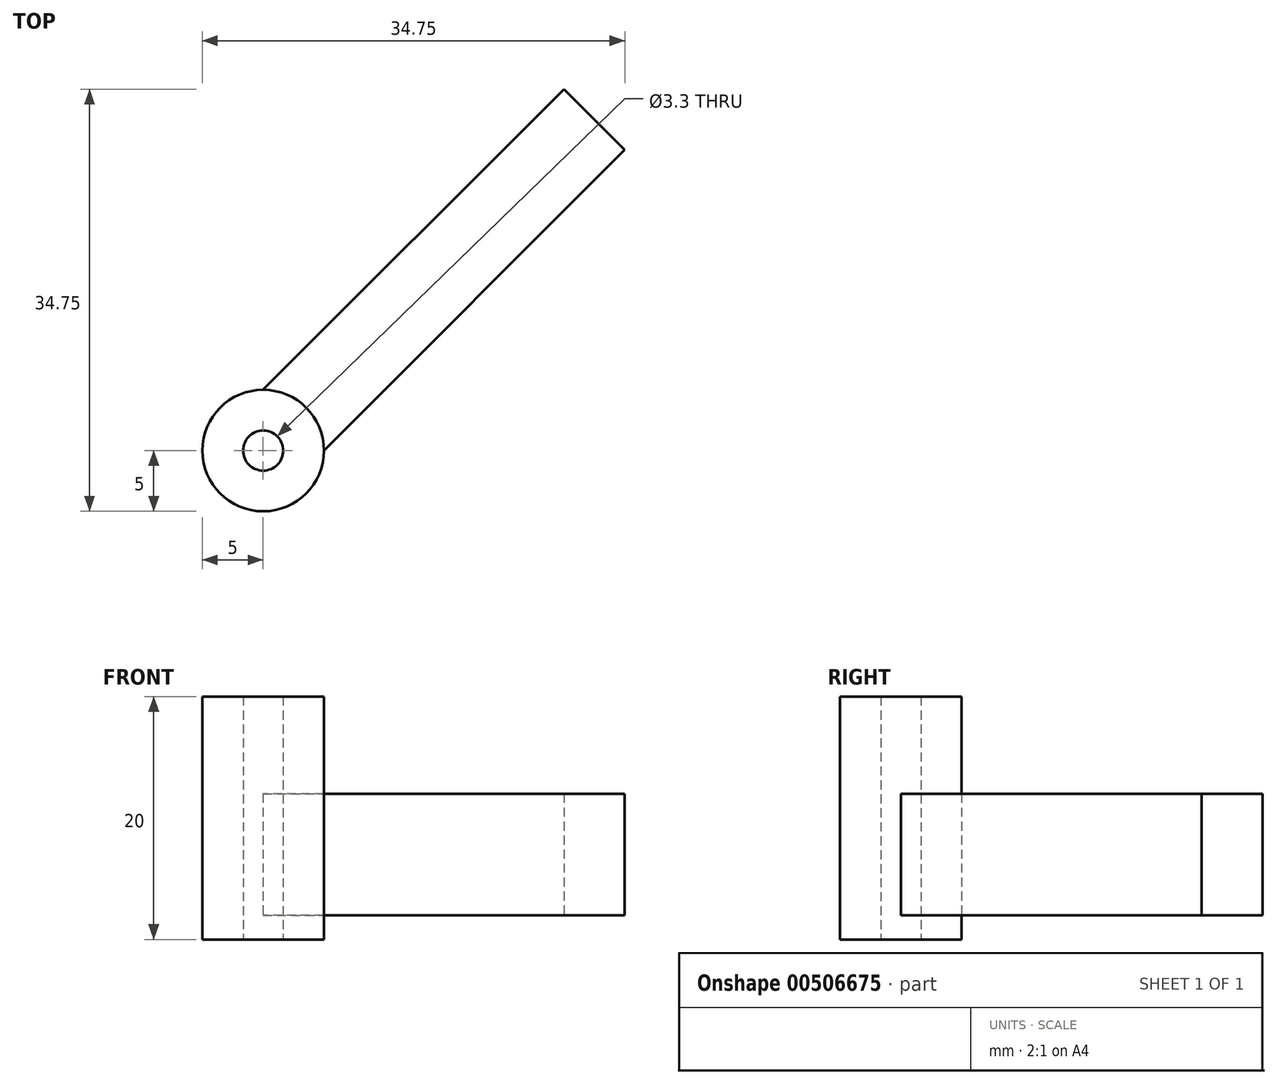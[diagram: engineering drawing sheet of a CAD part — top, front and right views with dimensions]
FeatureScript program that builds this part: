
annotation { "Feature Type Name" : "Feature", "Feature Type Description" : "" }
export const myFeature = defineFeature(function(context is Context, id is Id, definition is map)
    precondition{}
    {
        {
            var Q0;
            Q0=qCreatedBy(makeId("Top.planeOp"),FACE);
            var sketch = newSketch(context, id + "F0", { "sketchPlane" : qUnion([Q0])});
            skCircle(sketch, "E0", {"center": v(0, 0) * mm, "radius": 5 * mm});
            skPoint(sketch, "E1", {"position": v(0, 5) * mm});
            skPoint(sketch, "E2", {"position": v(5, 0) * mm});
            skLineSegment(sketch, "E3", {"start": v(0, 5) * mm, "end": v(24.75, 29.75) * mm});
            skLineSegment(sketch, "E4", {"start": v(0, 0) * mm, "end": v(8.55, 0) * mm});
            skLineSegment(sketch, "E5", {"start": v(5, 0) * mm, "end": v(29.75, 24.75) * mm});
            skLineSegment(sketch, "E6", {"start": v(0, 0) * mm, "end": v(9.63, 9.63) * mm});
            skLineSegment(sketch, "E7", {"start": v(0, 0) * mm, "end": v(0, 14.32) * mm});
            skLineSegment(sketch, "E8", {"start": v(24.75, 29.75) * mm, "end": v(29.75, 24.75) * mm});
            skSolve(sketch);
        }
        {
            var Q0;
            {var subQ0=sQuery(id+"F0.wireOp",EDGE,"E7");var subQ1=sQuery(id+"F0.wireOp",EDGE,"E0");var subQ2=makeQuery(id+"F0.imprint","INTERSECT",VERTEX,{"derivedFrom":[subQ1,sQuery(id+"F0.wireOp",EDGE,"E3"),subQ0]});Q0=makeQuery(id+"F0.imprint","IMPRINT",FACE,{"disambiguationData":[TD([[makeQuery(id+"F0.imprint","IMPRINT",EDGE,{"disambiguationData":[TD([[subQ2,-1.0]])],"derivedFrom":subQ1}),1.0]])]});}
            var Q1;
            {var subQ1=sQuery(id+"F0.wireOp",EDGE,"E0");var subQ3=sQuery(id+"F0.wireOp",EDGE,"E6");var subQ4=makeQuery(id+"F0.imprint","INTERSECT",VERTEX,{"derivedFrom":[subQ1,subQ3]});Q1=makeQuery(id+"F0.imprint","IMPRINT",FACE,{"disambiguationData":[TD([[makeQuery(id+"F0.imprint","IMPRINT",EDGE,{"disambiguationData":[TD([[subQ4,1.0]])],"derivedFrom":subQ1}),1.0]])]});}
            var Q2;
            {var subQ1=sQuery(id+"F0.wireOp",EDGE,"E0");var subQ3=sQuery(id+"F0.wireOp",EDGE,"E6");var subQ4=makeQuery(id+"F0.imprint","INTERSECT",VERTEX,{"derivedFrom":[subQ1,subQ3]});Q2=makeQuery(id+"F0.imprint","IMPRINT",FACE,{"disambiguationData":[TD([[makeQuery(id+"F0.imprint","IMPRINT",EDGE,{"disambiguationData":[TD([[subQ4,-1.0]])],"derivedFrom":subQ1}),1.0]])]});}
            extrude(context, id + "F1", {"entities" : qUnion([Q0, Q1, Q2]), "depth" : 20 * mm});
        }
        {
            var Q0;
            {var subQ0=sQuery(id+"F0.wireOp",EDGE,"E3");Q0=makeQuery(id+"F0.imprint","IMPRINT",FACE,{"disambiguationData":[TD([[makeQuery(id+"F0.imprint","IMPRINT",EDGE,{"derivedFrom":subQ0}),-1.0]])]});}
            extrude(context, id + "F2", {"entities" : qUnion([Q0]), "operationType" : NewBodyOperationType.ADD, "depth" : 12 * mm});
        }
        {
            var Q0;
            {var subQ0=sQuery(id+"F0.wireOp",EDGE,"E3");Q0=makeQuery(id+"F0.imprint","IMPRINT",FACE,{"disambiguationData":[TD([[makeQuery(id+"F0.imprint","IMPRINT",EDGE,{"derivedFrom":subQ0}),-1.0]])]});}
            extrude(context, id + "F3", {"entities" : qUnion([Q0]), "operationType" : NewBodyOperationType.REMOVE, "depth" : 2 * mm});
        }
        {
            var Q0;
            Q0=sQuery(id+"F0.wireOp",VERTEX,"E0.center");
            var Q1;
            Q1=makeQuery(id+"F1.opExtrude","SWEPT_BODY",BODY,{"disambiguationData":[OSD([sQuery(id+"F0.wireOp",EDGE,"E0")])]});
            hole(context, id + "F4", {"style" : HoleStyle.SIMPLE, "endStyle" : HoleEndStyle.THROUGH, "oppositeDirection" : true, "holeDiameter" : 3.3 * mm, "tappedDepth" : 12 * mm, "tapClearance" : 3, "locations" : qUnion([Q0]), "scope" : qUnion([Q1])});
        }
    });
